# Revit family: JC KONTAKTER JCK211 DE
name_source: partatom
category: Specialty Equipment
units: mm (PartAtom-declared; Revit-internal decimal feet)

## family parameters
Cut with Voids When Loaded = No
Enable Cutting in Views = Yes
Host = Face
Maintain Annotation Orientation = Yes
Part Type = Normal
Room Calculation Point = No
Round Connector Dimension = Use Diameter
Shared = No

## types (1)
- JCK211
    Anzahl der mikroschalter = 1
    CE-kennzeichnung = https://jckontakter.se
    Deckel = ABS 750SW (schwarz)
    Default Elevation = 800 mm  [stored 2.62467 ft]
    Description = Dieser Großflächentaster ist aus schlagfestem ABS-Kunststoff hergestellt. Er hat eine konvexe Tastfläche mit Tastlinien, die angeben, wo der Taster gedrückt werden soll. Dieses Modell bietet eine weiße Tastfläche und einen weißen Rahmen. Vor allem für den Einsatz in Innenbereichen konzipiert, kann aber auch im Freien eingesetzt werden, da er mit einem feuchtigkeitsgeschützten Mikroschalter der IP-Klasse 67 ausgerüstet ist.
    Geringster nennstrom = 1mA/4 V DC
    Herstellungsland = Schweden
    Kern = ABS 750SW (weiss)
    Manufacturer = JC kontakter
    Mikroschalter = Standard NO IP67
    Model = JCK211
    Nomineller nennstrom = 12 V - Resistive 6A Inductive L/R 5ms 6A, 24 V - Resistive 6A Inductive L/R 5ms 5A
    Produktgewicht = 0.230 kg.
    Technisches Produktblatt = https://grossflaechentaster.de
    URL = https://grossflaechentaster.de

note: [stored X ft] marks values corroborated as IEEE doubles in the binary element streams (Revit-internal decimal feet)

## geometry (parser evidence)
native form markers: Sweep x5
no freeform markers — native parametric forms only
